# Revit family: Mi-600
name_source: partatom
category: Plumbing Fixtures
revit_build: Autodesk Revit Structure 2013 (Build: 20120221_2030(x64)
units: mm (PartAtom-declared; Revit-internal decimal feet)

## types (3) — shared parameters
Body Material = ABS Plastic
Description = P-Trap Seal Primer Connector
Model = MI-600
URL = www.mifab.com

## per-type parameters (varying)
| type | Connection | Diameter Diff. | Fitting value | Height | Manufacturer | Pipe size | Upper Height | connection dia | connection inner sia |
| MI-600(3) | 1' - 11 13/32" | 0' - 7 3/16" | 1' - 7 13/16" | 5' - 9" | Mifab | 1' - 6" | 2' - 6" | 0' - 4 1/2" | 0' - 3 15/32" |
| MI-600(2) | 1' - 3 19/32" | 0' - 4 13/16" | 1' - 1 3/16" | 4' - 0" | Mifab | 1' - 0" | 1' - 8 7/8" | 0' - 3" | 0' - 2 5/16" |
| MI-600(4) | 2' - 7 3/16" | 0' - 9 19/32" | 2' - 2 13/32" | 8' - 0" | MIfab | 2' - 0" | 3' - 5 3/4" | 0' - 6" | 0' - 4 5/8" |

## geometry (parser evidence)
native form markers: Blend x4, Sweep x1
no freeform markers — native parametric forms only
